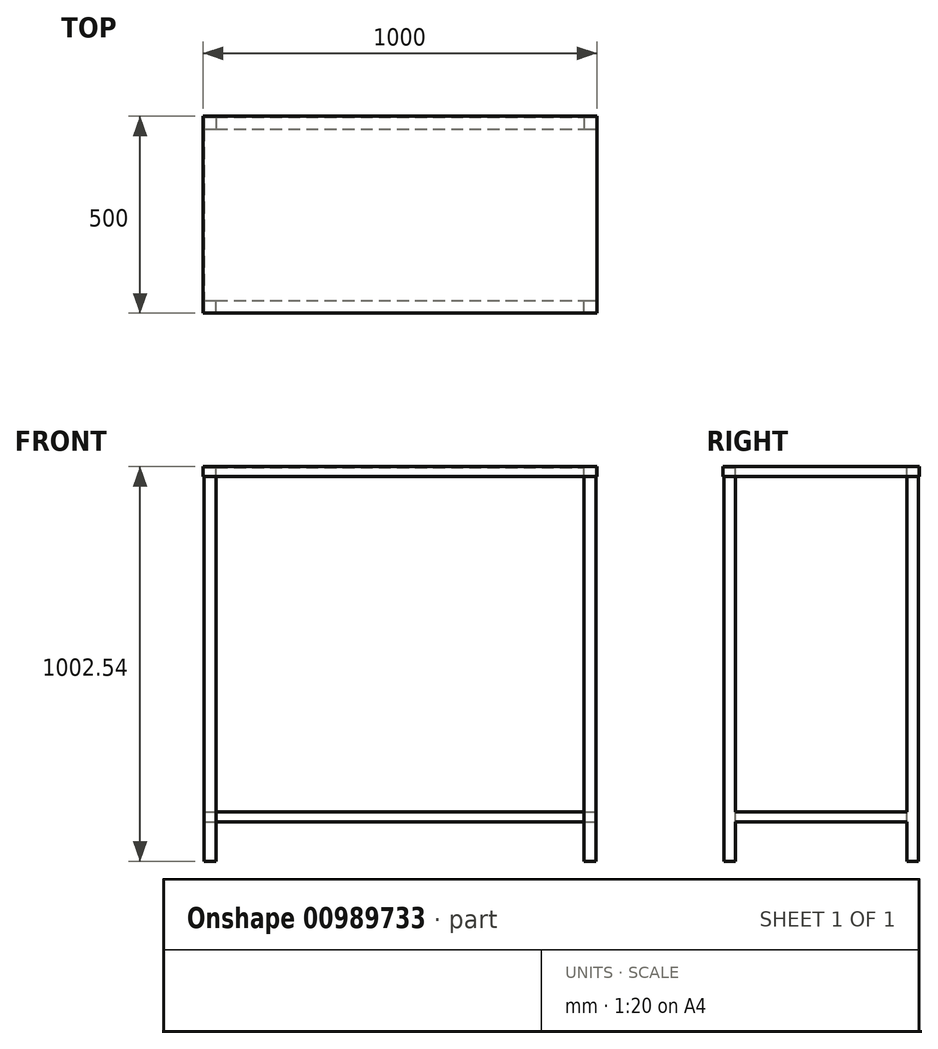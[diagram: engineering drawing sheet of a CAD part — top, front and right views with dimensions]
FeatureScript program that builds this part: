
annotation { "Feature Type Name" : "Feature", "Feature Type Description" : "" }
export const myFeature = defineFeature(function(context is Context, id is Id, definition is map)
    precondition{}
    {
        {
            var Q0;
            Q0=qCreatedBy(makeId("Top.planeOp"),FACE);
            var sketch = newSketch(context, id + "F0", { "sketchPlane" : qUnion([Q0])});
            skLineSegment(sketch, "E0.bottom", {"start": v(-500, 250) * mm, "end": v(500, 250) * mm});
            skLineSegment(sketch, "E0.top", {"start": v(-500, -250) * mm, "end": v(500, -250) * mm});
            skLineSegment(sketch, "E0.left", {"start": v(-500, 250) * mm, "end": v(-500, -250) * mm});
            skLineSegment(sketch, "E0.right", {"start": v(500, 250) * mm, "end": v(500, -250) * mm});
            skLineSegment(sketch, "E1", {"start": v(0, 410.22) * mm, "end": v(0, -377.07) * mm, "construction": true});
            skLineSegment(sketch, "E2", {"start": v(-526.24, 0) * mm, "end": v(595.3, 0) * mm, "construction": true});
            skSolve(sketch);
        }
        {
            var Q0;
            Q0 = qSketchRegion(id + "F0", true);
            extrude(context, id + "F1", {"entities" : qUnion([Q0]), "depth" : 25.4 * mm, "offsetDistance" : 25.4 * mm});
        }
        {
            var Q0;
            Q0=makeQuery(id+"F1.opExtrude","CAP_FACE",FACE,{"disambiguationData":[OSD([sQuery(id+"F0.wireOp",EDGE,"E0.bottom"),sQuery(id+"F0.wireOp",EDGE,"E0.top"),sQuery(id+"F0.wireOp",EDGE,"E0.left"),sQuery(id+"F0.wireOp",EDGE,"E0.right")])],"isStart":true});
            shell(context, id + "F2", {"entities" : qUnion([Q0]), "thickness" : 2.54 * mm});
        }
        {
            var Q0;
            Q0=makeQuery(id+"F2.opShell","OFFSET_FACE",FACE,{"disambiguationData":[OSD([sQuery(id+"F0.wireOp",EDGE,"E0.bottom"),sQuery(id+"F0.wireOp",EDGE,"E0.top"),sQuery(id+"F0.wireOp",EDGE,"E0.left"),sQuery(id+"F0.wireOp",EDGE,"E0.right")])]});
            var sketch = newSketch(context, id + "F3", { "sketchPlane" : qUnion([Q0])});
            skLineSegment(sketch, "E3.bottom", {"start": v(-497.46, 247.46) * mm, "end": v(-467.46, 247.46) * mm});
            skLineSegment(sketch, "E3.top", {"start": v(-497.46, 217.46) * mm, "end": v(-467.46, 217.46) * mm});
            skLineSegment(sketch, "E3.left", {"start": v(-497.46, 247.46) * mm, "end": v(-497.46, 217.46) * mm});
            skLineSegment(sketch, "E3.right", {"start": v(-467.46, 247.46) * mm, "end": v(-467.46, 217.46) * mm});
            skLineSegment(sketch, "E4.bottom", {"start": v(-497.46, -247.46) * mm, "end": v(-467.46, -247.46) * mm});
            skLineSegment(sketch, "E4.top", {"start": v(-497.46, -217.46) * mm, "end": v(-467.46, -217.46) * mm});
            skLineSegment(sketch, "E4.left", {"start": v(-497.46, -247.46) * mm, "end": v(-497.46, -217.46) * mm});
            skLineSegment(sketch, "E4.right", {"start": v(-467.46, -247.46) * mm, "end": v(-467.46, -217.46) * mm});
            skLineSegment(sketch, "E5.bottom", {"start": v(497.46, 247.46) * mm, "end": v(467.46, 247.46) * mm});
            skLineSegment(sketch, "E5.top", {"start": v(497.46, 217.46) * mm, "end": v(467.46, 217.46) * mm});
            skLineSegment(sketch, "E5.left", {"start": v(497.46, 247.46) * mm, "end": v(497.46, 217.46) * mm});
            skLineSegment(sketch, "E5.right", {"start": v(467.46, 247.46) * mm, "end": v(467.46, 217.46) * mm});
            skLineSegment(sketch, "E6.bottom", {"start": v(497.46, -247.46) * mm, "end": v(467.46, -247.46) * mm});
            skLineSegment(sketch, "E6.top", {"start": v(497.46, -217.46) * mm, "end": v(467.46, -217.46) * mm});
            skLineSegment(sketch, "E6.left", {"start": v(497.46, -247.46) * mm, "end": v(497.46, -217.46) * mm});
            skLineSegment(sketch, "E6.right", {"start": v(467.46, -247.46) * mm, "end": v(467.46, -217.46) * mm});
            skSolve(sketch);
        }
        {
            var Q0;
            Q0 = qSketchRegion(id + "F3", true);
            extrude(context, id + "F4", {"entities" : qUnion([Q0]), "operationType" : NewBodyOperationType.ADD, "depth" : 1000 * mm, "offsetDistance" : 25.4 * mm});
        }
        {
            var Q0;
            Q0=makeQuery(id+"F4.opExtrude","CAP_FACE",FACE,{"disambiguationData":[OSD([sQuery(id+"F3.wireOp",EDGE,"E3.bottom"),sQuery(id+"F3.wireOp",EDGE,"E3.top"),sQuery(id+"F3.wireOp",EDGE,"E3.left"),sQuery(id+"F3.wireOp",EDGE,"E3.right")])],"isStart":false});
            cPlane(context, id + "F5", {"entities" : qUnion([Q0]), "cplaneType" : CPlaneType.OFFSET, "offset" : 100 * mm, "oppositeDirection" : true, "width" : 152.4 * mm, "height" : 152.4 * mm});
        }
        {
            var Q0;
            Q0=qCreatedBy(id+"F5.planeOp",FACE);
            var sketch = newSketch(context, id + "F6", { "sketchPlane" : qUnion([Q0])});
            skLineSegment(sketch, "E7.bottom", {"start": v(-497.46, 217.46) * mm, "end": v(497.46, 217.46) * mm});
            skLineSegment(sketch, "E7.top", {"start": v(-497.46, -217.46) * mm, "end": v(497.46, -217.46) * mm});
            skLineSegment(sketch, "E7.left", {"start": v(-497.46, 217.46) * mm, "end": v(-497.46, -217.46) * mm});
            skLineSegment(sketch, "E7.right", {"start": v(497.46, 217.46) * mm, "end": v(497.46, -217.46) * mm});
            skSolve(sketch);
        }
        {
            var Q0;
            Q0 = qSketchRegion(id + "F6", true);
            extrude(context, id + "F7", {"entities" : qUnion([Q0]), "operationType" : NewBodyOperationType.ADD, "oppositeDirection" : true, "depth" : 25.4 * mm, "offsetDistance" : 25.4 * mm});
        }
    });
